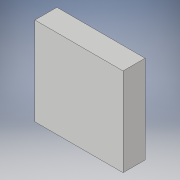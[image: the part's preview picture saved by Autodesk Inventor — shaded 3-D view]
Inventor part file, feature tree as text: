
AUTODESK INVENTOR PART (.ipt)
format: ipt  version: 2018 (Build 220112000, 112)  size: 87,552 bytes
history: native  units: in
note: dims shown in document units (in); Inventor stores cm internally (conversion verified against a paired STEP export)
features: extrude x1, sketch x1
ambient origin geometry x8: Origin, YZ Plane, XZ Plane, XY Plane, X Axis, Y Axis, Z Axis, Center Point
bodies: Solid1 (feature_tree)
feature tree (2):
  extrude  "Extrusion1"  Depth=4.0in
  sketch  "Sketch1"  dims[d0=4.0in d1=4.0in d2=1.0in d3=0.0in]
